# Revit family: TOPAC
name_source: partatom
category: Plumbing Fixtures
revit_build: Autodesk Revit 2015 (Build: 20140905_0730(x64)
units: mm (PartAtom-declared; Revit-internal decimal feet)

## types (36) — shared parameters
Aluminum = Aluminum
Glass = Glass
Manufacturer = SanSwiss
Model = TOPAC
Profile = Profile
Seal = Seal
Type Comments = TOP LINE
URL = http://www.sanswiss.com

## per-type parameters (varying)
| type | TOP D | TOP G | a1 | a2 |
| 700x700 | TOP D : 700 | TOP G : 700 | 700 mm  [stored 2.29659 ft] | 700 mm  [stored 2.29659 ft] |
| 700x750 | TOP D : 700 | TOP G : 750 | 700 mm  [stored 2.29659 ft] | 750 mm  [stored 2.46063 ft] |
| 1200x1200 | TOP D : 1200 | TOP G : 1200 | 1200 mm | 1200 mm |
| 1200x1000 | TOP D : 1200 | TOP G : 1000 | 1200 mm | 1000 mm  [stored 3.28084 ft] |
| 1200x900 | TOP D : 1200 | TOP G : 900 | 1200 mm | 900 mm  [stored 2.95276 ft] |
| 1200x800 | TOP D : 1200 | TOP G : 800 | 1200 mm | 800 mm  [stored 2.62467 ft] |
| 1200x750 | TOP D : 1200 | TOP G : 750 | 1200 mm | 750 mm  [stored 2.46063 ft] |
| 1200x700 | TOP D : 1200 | TOP G : 700 | 1200 mm | 700 mm  [stored 2.29659 ft] |
| 1000x1200 | TOP D : 1000 | TOP G : 1200 | 1000 mm  [stored 3.28084 ft] | 1200 mm |
| 1000x1000 | TOP D : 1000 | TOP G : 1000 | 1000 mm  [stored 3.28084 ft] | 1000 mm  [stored 3.28084 ft] |
| 1000x900 | TOP D : 1000 | TOP G : 900 | 1000 mm  [stored 3.28084 ft] | 900 mm  [stored 2.95276 ft] |
| 1000x800 | TOP D : 1000 | TOP G : 800 | 1000 mm  [stored 3.28084 ft] | 800 mm  [stored 2.62467 ft] |
| 1000x750 | TOP D : 1000 | TOP G : 750 | 1000 mm  [stored 3.28084 ft] | 750 mm  [stored 2.46063 ft] |
| 1000x700 | TOP D : 1000 | TOP G : 700 | 1000 mm  [stored 3.28084 ft] | 700 mm  [stored 2.29659 ft] |
| 900x1200 | TOP D : 900 | TOP G : 1200 | 900 mm  [stored 2.95276 ft] | 1200 mm |
| 900x1000 | TOP D : 900 | TOP G : 1000 | 900 mm  [stored 2.95276 ft] | 1000 mm  [stored 3.28084 ft] |
| 900x900 | TOP D : 900 | TOP G : 900 | 900 mm  [stored 2.95276 ft] | 900 mm  [stored 2.95276 ft] |
| 900x800 | TOP D : 900 | TOP G : 800 | 900 mm  [stored 2.95276 ft] | 800 mm  [stored 2.62467 ft] |
| 900x750 | TOP D : 900 | TOP G : 750 | 900 mm  [stored 2.95276 ft] | 750 mm  [stored 2.46063 ft] |
| 900x700 | TOP D : 900 | TOP G : 700 | 900 mm  [stored 2.95276 ft] | 700 mm  [stored 2.29659 ft] |
| 800x1200 | TOP D : 800 | TOP G : 1200 | 800 mm  [stored 2.62467 ft] | 1200 mm |
| 800x1000 | TOP D : 800 | TOP G : 1000 | 800 mm  [stored 2.62467 ft] | 1000 mm  [stored 3.28084 ft] |
| 800x900 | TOP D : 800 | TOP G : 900 | 800 mm  [stored 2.62467 ft] | 900 mm  [stored 2.95276 ft] |
| 800x800 | TOP D : 800 | TOP G : 800 | 800 mm  [stored 2.62467 ft] | 800 mm  [stored 2.62467 ft] |
| 800x750 | TOP D : 800 | TOP G : 750 | 800 mm  [stored 2.62467 ft] | 750 mm  [stored 2.46063 ft] |
| 800x700 | TOP D : 800 | TOP G : 700 | 800 mm  [stored 2.62467 ft] | 700 mm  [stored 2.29659 ft] |
| 750x1200 | TOP D : 750 | TOP G : 1200 | 750 mm  [stored 2.46063 ft] | 1200 mm |
| 750x1000 | TOP D : 750 | TOP G : 1000 | 750 mm  [stored 2.46063 ft] | 1000 mm  [stored 3.28084 ft] |
| 750x900 | TOP D : 750 | TOP G : 900 | 750 mm  [stored 2.46063 ft] | 900 mm  [stored 2.95276 ft] |
| 750x800 | TOP D : 750 | TOP G : 800 | 750 mm  [stored 2.46063 ft] | 800 mm  [stored 2.62467 ft] |
| 750x750 | TOP D : 750 | TOP G : 750 | 750 mm  [stored 2.46063 ft] | 750 mm  [stored 2.46063 ft] |
| 750x700 | TOP D : 750 | TOP G : 700 | 750 mm  [stored 2.46063 ft] | 700 mm  [stored 2.29659 ft] |
| 700x1200 | TOP D : 700 | TOP G : 1200 | 700 mm  [stored 2.29659 ft] | 1200 mm |
| 700x1000 | TOP D : 700 | TOP G : 1000 | 700 mm  [stored 2.29659 ft] | 1000 mm  [stored 3.28084 ft] |
| 700x800 | TOP D : 700 | TOP G : 800 | 700 mm  [stored 2.29659 ft] | 800 mm  [stored 2.62467 ft] |
| 700x900 | TOP D : 700 | TOP G : 900 | 700 mm  [stored 2.29659 ft] | 900 mm  [stored 2.95276 ft] |

note: [stored X ft] marks values corroborated as IEEE doubles in the binary element streams (Revit-internal decimal feet)

## geometry (parser evidence)
native form markers: Blend x8, Sweep x23
no freeform markers — native parametric forms only
